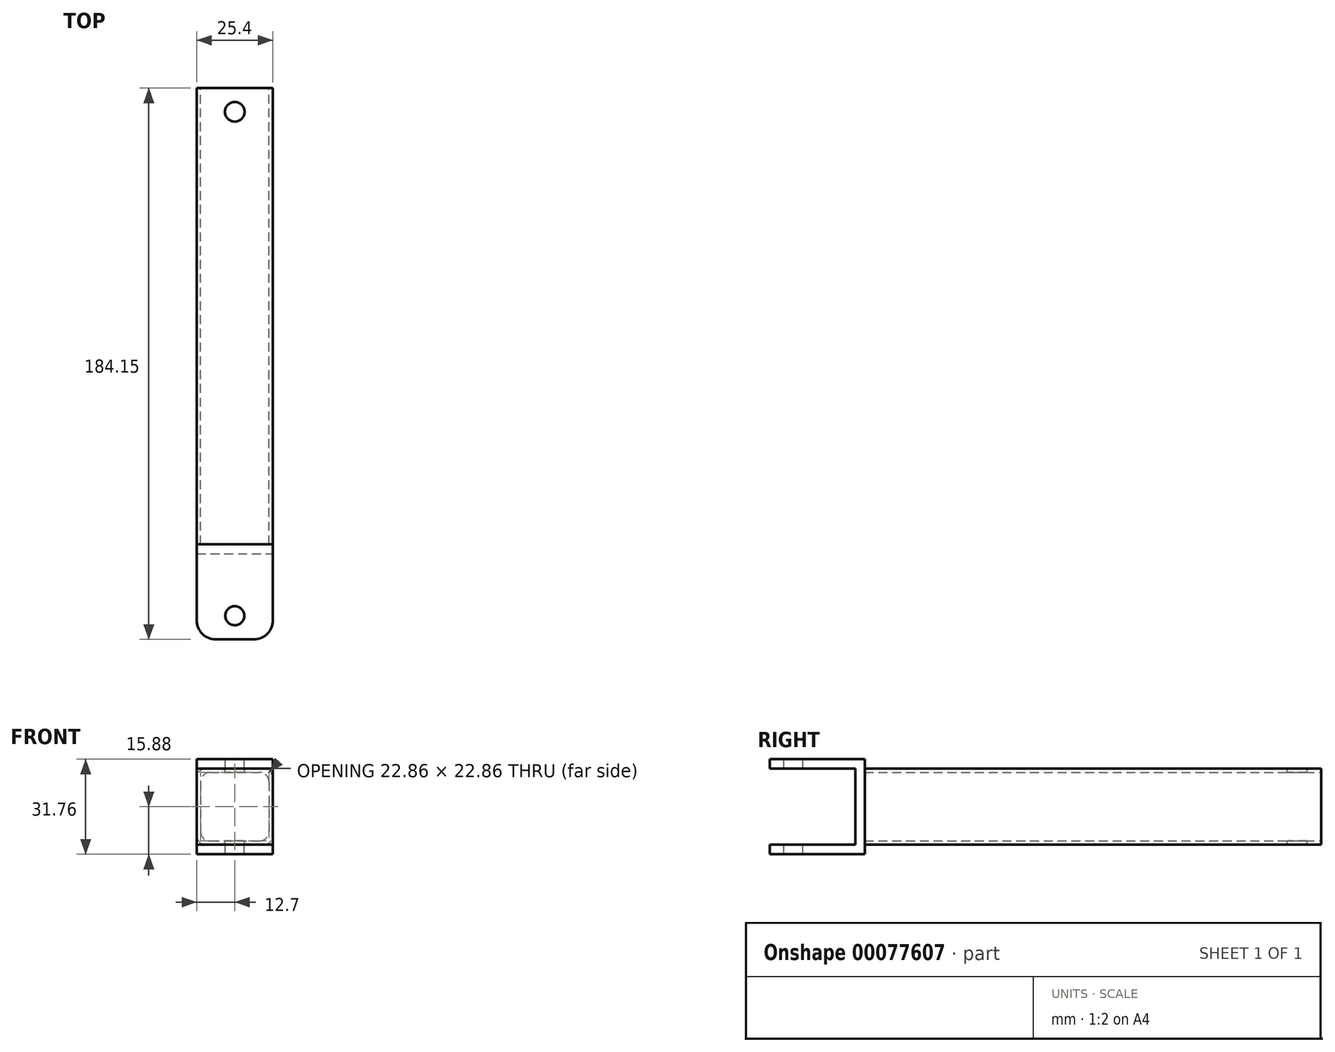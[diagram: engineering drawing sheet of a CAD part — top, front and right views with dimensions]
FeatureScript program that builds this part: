
annotation { "Feature Type Name" : "Feature", "Feature Type Description" : "" }
export const myFeature = defineFeature(function(context is Context, id is Id, definition is map)
    precondition{}
    {
        {
            var Q0;
            Q0=qCreatedBy(makeId("Front.planeOp"),FACE);
            var sketch = newSketch(context, id + "F0", { "sketchPlane" : qUnion([Q0])});
            skLineSegment(sketch, "E0.bottom", {"start": v(-12.7, 12.7) * mm, "end": v(12.7, 12.7) * mm});
            skLineSegment(sketch, "E0.top", {"start": v(-12.7, -12.7) * mm, "end": v(12.7, -12.7) * mm});
            skLineSegment(sketch, "E0.left", {"start": v(-12.7, 12.7) * mm, "end": v(-12.7, -12.7) * mm});
            skLineSegment(sketch, "E0.right", {"start": v(12.7, 12.7) * mm, "end": v(12.7, -12.7) * mm});
            skLineSegment(sketch, "E1.0", {"start": v(-11.43, 11.43) * mm, "end": v(11.43, 11.43) * mm});
            skLineSegment(sketch, "E1.1", {"start": v(-11.43, 11.43) * mm, "end": v(-11.43, -11.43) * mm});
            skLineSegment(sketch, "E1.2", {"start": v(-11.43, -11.43) * mm, "end": v(11.43, -11.43) * mm});
            skLineSegment(sketch, "E1.3", {"start": v(11.43, 11.43) * mm, "end": v(11.43, -11.43) * mm});
            skSolve(sketch);
        }
        {
            var Q0;
            Q0 = qSketchRegion(id + "F0", true);
            extrude(context, id + "F1", {"entities" : qUnion([Q0]), "depth" : 152.4 * mm});
        }
        {
            var Q0;
            Q0=makeQuery(id+"F1.opExtrude","SWEPT_EDGE",EDGE,{"disambiguationData":[OSD([sQuery(id+"F0.wireOp",EDGE,"E0.bottom"),sQuery(id+"F0.wireOp",EDGE,"E0.right")])]});
            var Q1;
            Q1=makeQuery(id+"F1.opExtrude","SWEPT_EDGE",EDGE,{"disambiguationData":[OSD([sQuery(id+"F0.wireOp",EDGE,"E0.bottom"),sQuery(id+"F0.wireOp",EDGE,"E0.left")])]});
            var Q2;
            Q2=makeQuery(id+"F1.opExtrude","SWEPT_EDGE",EDGE,{"disambiguationData":[OSD([sQuery(id+"F0.wireOp",EDGE,"E0.top"),sQuery(id+"F0.wireOp",EDGE,"E0.right")])]});
            var Q3;
            Q3=makeQuery(id+"F1.opExtrude","SWEPT_EDGE",EDGE,{"disambiguationData":[OSD([sQuery(id+"F0.wireOp",EDGE,"E0.top"),sQuery(id+"F0.wireOp",EDGE,"E0.left")])]});
            var Q4;
            Q4=makeQuery(id+"F1.opExtrude","SWEPT_EDGE",EDGE,{"disambiguationData":[OSD([sQuery(id+"F0.wireOp",EDGE,"E1.0"),sQuery(id+"F0.wireOp",EDGE,"E1.3")])]});
            var Q5;
            Q5=makeQuery(id+"F1.opExtrude","SWEPT_EDGE",EDGE,{"disambiguationData":[OSD([sQuery(id+"F0.wireOp",EDGE,"E1.2"),sQuery(id+"F0.wireOp",EDGE,"E1.3")])]});
            var Q6;
            Q6=makeQuery(id+"F1.opExtrude","SWEPT_EDGE",EDGE,{"disambiguationData":[OSD([sQuery(id+"F0.wireOp",EDGE,"E1.0"),sQuery(id+"F0.wireOp",EDGE,"E1.1")])]});
            var Q7;
            Q7=makeQuery(id+"F1.opExtrude","SWEPT_EDGE",EDGE,{"disambiguationData":[OSD([sQuery(id+"F0.wireOp",EDGE,"E1.1"),sQuery(id+"F0.wireOp",EDGE,"E1.2")])]});
            fillet(context, id + "F2", {"entities" : qUnion([Q0, Q1, Q2, Q3, Q4, Q5, Q6, Q7]), "radius" : 3.17 * mm, "tangentPropagation" : true, "allowEdgeOverflow" : false});
        }
        {
            var Q0;
            Q0=makeQuery(id+"F1.opExtrude","SWEPT_FACE",FACE,{"disambiguationData":[OSD([sQuery(id+"F0.wireOp",EDGE,"E0.bottom")])]});
            var sketch = newSketch(context, id + "F3", { "sketchPlane" : qUnion([Q0])});
            skCircle(sketch, "E2", {"center": v(0, -7.92) * mm, "radius": 3.28 * mm});
            skSolve(sketch);
        }
        {
            var Q0;
            Q0 = qSketchRegion(id + "F3", true);
            extrude(context, id + "F4", {"entities" : qUnion([Q0]), "operationType" : NewBodyOperationType.REMOVE, "endBound" : BoundingType.THROUGH_ALL, "oppositeDirection" : true, "depth" : 25.4 * mm});
        }
        {
            var Q0;
            Q0=makeQuery(id+"F1.opExtrude","SWEPT_FACE",FACE,{"disambiguationData":[OSD([sQuery(id+"F0.wireOp",EDGE,"E0.right")])]});
            var sketch = newSketch(context, id + "F5", { "sketchPlane" : qUnion([Q0])});
            skLineSegment(sketch, "E3.bottom", {"start": v(-152.4, -15.88) * mm, "end": v(-184.15, -15.88) * mm});
            skLineSegment(sketch, "E3.top", {"start": v(-152.4, 15.87) * mm, "end": v(-184.15, 15.87) * mm});
            skLineSegment(sketch, "E3.left", {"start": v(-152.4, -15.88) * mm, "end": v(-152.4, 15.87) * mm});
            skLineSegment(sketch, "E3.right", {"start": v(-184.15, -15.88) * mm, "end": v(-184.15, -12.7) * mm});
            skLineSegment(sketch, "E4.0", {"start": v(-155.58, 12.7) * mm, "end": v(-184.15, 12.7) * mm});
            skLineSegment(sketch, "E4.1", {"start": v(-155.58, -12.7) * mm, "end": v(-155.58, 12.7) * mm});
            skLineSegment(sketch, "E4.2", {"start": v(-155.58, -12.7) * mm, "end": v(-184.15, -12.7) * mm});
            skLineSegment(sketch, "E5.trimOffspring", {"start": v(-184.15, 12.7) * mm, "end": v(-184.15, 15.87) * mm});
            skSolve(sketch);
        }
        {
            var Q0;
            Q0 = qSketchRegion(id + "F5", true);
            extrude(context, id + "F6", {"entities" : qUnion([Q0]), "oppositeDirection" : true, "depth" : 25.4 * mm});
        }
        {
            var Q0;
            Q0=makeQuery(id+"F6.opExtrude","SWEPT_FACE",FACE,{"disambiguationData":[OSD([sQuery(id+"F5.wireOp",EDGE,"E3.top")])]});
            var sketch = newSketch(context, id + "F7", { "sketchPlane" : qUnion([Q0])});
            skCircle(sketch, "E6", {"center": v(0, -176.23) * mm, "radius": 3.18 * mm});
            skPoint(sketch, "E6.centerSnap0", {"position": v(0, -184.15) * mm});
            skSolve(sketch);
        }
        {
            var Q0;
            Q0 = qSketchRegion(id + "F7", true);
            extrude(context, id + "F8", {"entities" : qUnion([Q0]), "operationType" : NewBodyOperationType.REMOVE, "endBound" : BoundingType.THROUGH_ALL, "oppositeDirection" : true, "depth" : 25.4 * mm});
        }
        {
            var Q0;
            Q0=makeQuery(id+"F6.opExtrude","CAP_EDGE",EDGE,{"disambiguationData":[OSD([sQuery(id+"F5.wireOp",EDGE,"E5.trimOffspring")])],"isStart":true});
            var Q1;
            Q1=makeQuery(id+"F6.opExtrude","CAP_EDGE",EDGE,{"disambiguationData":[OSD([sQuery(id+"F5.wireOp",EDGE,"E5.trimOffspring")])],"isStart":false});
            var Q2;
            Q2=makeQuery(id+"F6.opExtrude","CAP_EDGE",EDGE,{"disambiguationData":[OSD([sQuery(id+"F5.wireOp",EDGE,"E3.right")])],"isStart":true});
            var Q3;
            Q3=makeQuery(id+"F6.opExtrude","CAP_EDGE",EDGE,{"disambiguationData":[OSD([sQuery(id+"F5.wireOp",EDGE,"E3.right")])],"isStart":false});
            fillet(context, id + "F9", {"entities" : qUnion([Q0, Q1, Q2, Q3]), "radius" : 6.35 * mm, "tangentPropagation" : true, "allowEdgeOverflow" : false});
        }
    });
